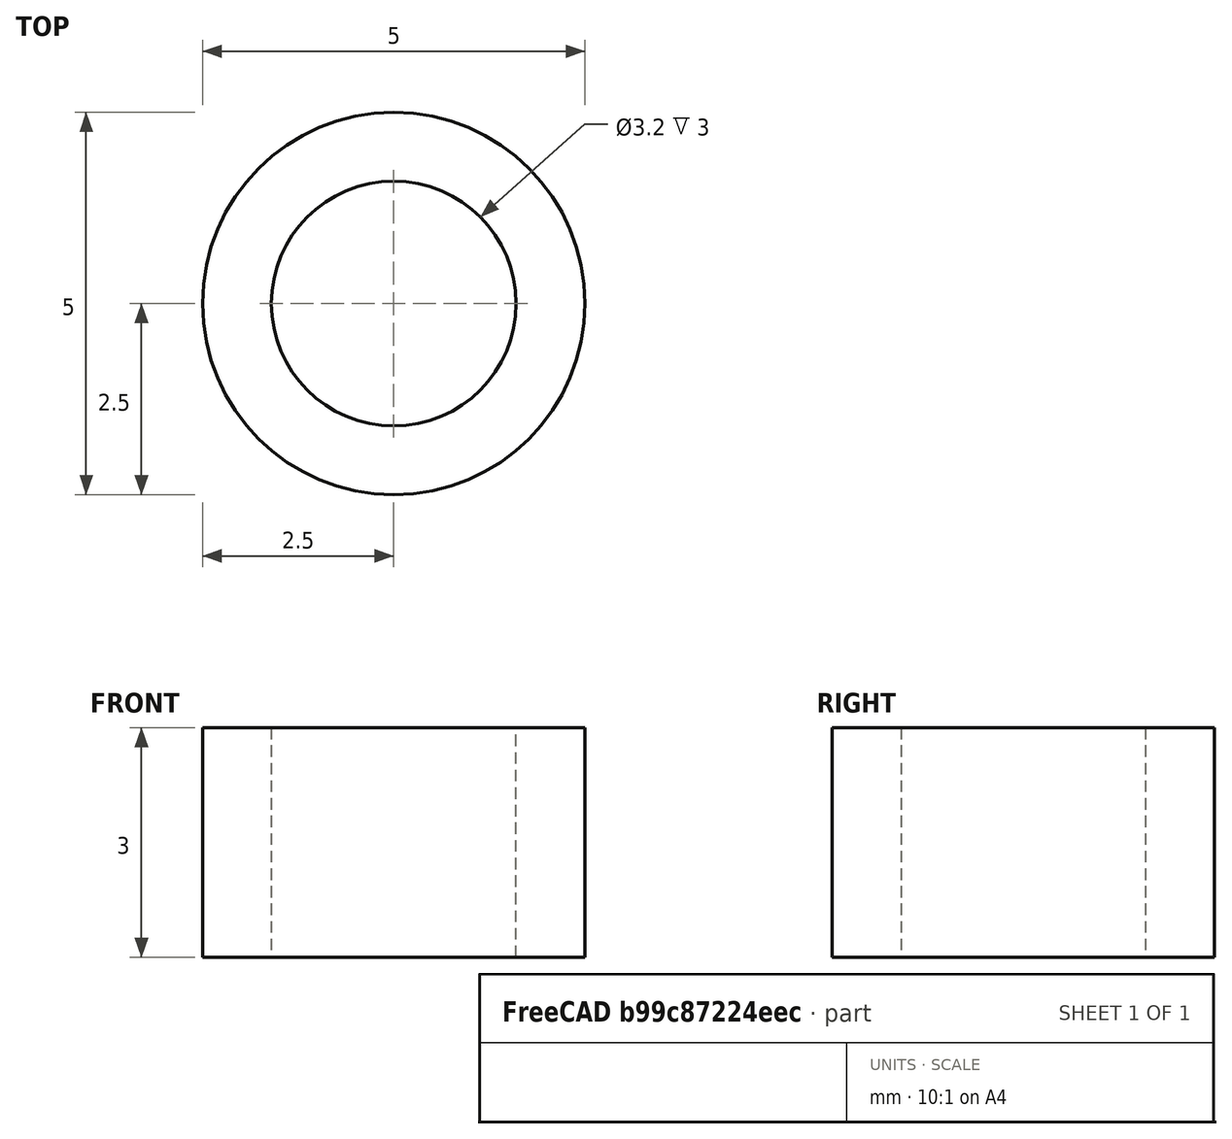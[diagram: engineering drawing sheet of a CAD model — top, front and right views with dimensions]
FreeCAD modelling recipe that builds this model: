
FCSTD DOCUMENT  (FreeCAD 2023.521R14555 (Git shallow))
Label: M3_spacer
License: All rights reserved
LicenseURL: https://en.wikipedia.org/wiki/All_rights_reserved
objects: Sketcher::SketchObject×1, PartDesign::Pad×1, PartDesign::Body×1
note: 6 computed .brp shape members not serialized (recipe doc carries the construction recipe); baked Part::Feature solids carry a one-line shape summary decoded from their .brp

FEATURE [Sketcher::SketchObject] Sketch
  ArcFitTolerance = 1e-06
  AttachmentSupport = -> [XY_Plane]
  ExternalBSplineMaxDegree = 5
  ExternalBSplineTolerance = 0.0001
  FixShape = 1
  FullyConstrained = true
  InternalTolerance = 1e-06
  InvalidShape = false
  MakeInternals = false
  MapMode = 5
  Support = -> [XY_Plane]
  TreeRank = 11
  ValidateShape = false
  sketch-geometry (2):
    g0: Circle CenterX=0 CenterY=0 CenterZ=0 NormalX=0 NormalY=0 NormalZ=1 AngleXU=0 Radius=1.6
    g1: Circle CenterX=0 CenterY=0 CenterZ=0 NormalX=0 NormalY=0 NormalZ=1 AngleXU=0 Radius=2.5
  constraints (4):
    c: Coincident(g0,g-1)
    c: Coincident(g1,g0)
    c: Diameter(g0) = 3.2
    c: Diameter(g1) = 5
FEATURE [PartDesign::Pad] Pad
  AddSubType = 0
  AlongSketchNormal = false
  AutoTaperInnerAngle = true
  CheckUpToFaceLimits = true
  ClaimChildren = false
  Direction = (0,0,1)
  Fit = 0
  FitJoin = 0
  FixShape = 1
  InnerFit = 0
  InnerFitJoin = 0
  InvalidShape = false
  Length = 3
  Length2 = 10
  Linearize = true
  NewSolid = false
  Profile = -> Sketch
  ReferenceAxis = -> Sketch [N_Axis]
  Refine = true
  Suppress = false
  TaperInnerAngle = 0
  TaperInnerAngleRev = 0
  TreeRank = 12
  Type = 0
  ValidateShape = true
  _ProfileBasedVersion = 1
FEATURE [PartDesign::Body] Body
  AutoGroupSolids = false
  ClaimAllChildren = false
  ExportMode = 0
  FixShape = 1
  Group = -> [Sketch,Pad]
  InvalidShape = false
  Origin = -> Origin
  Tip = -> Pad
  TreeRank = 10
  ValidateShape = false
  _ExportChildren = -> [Pad]
  _GroupVersion = 1
